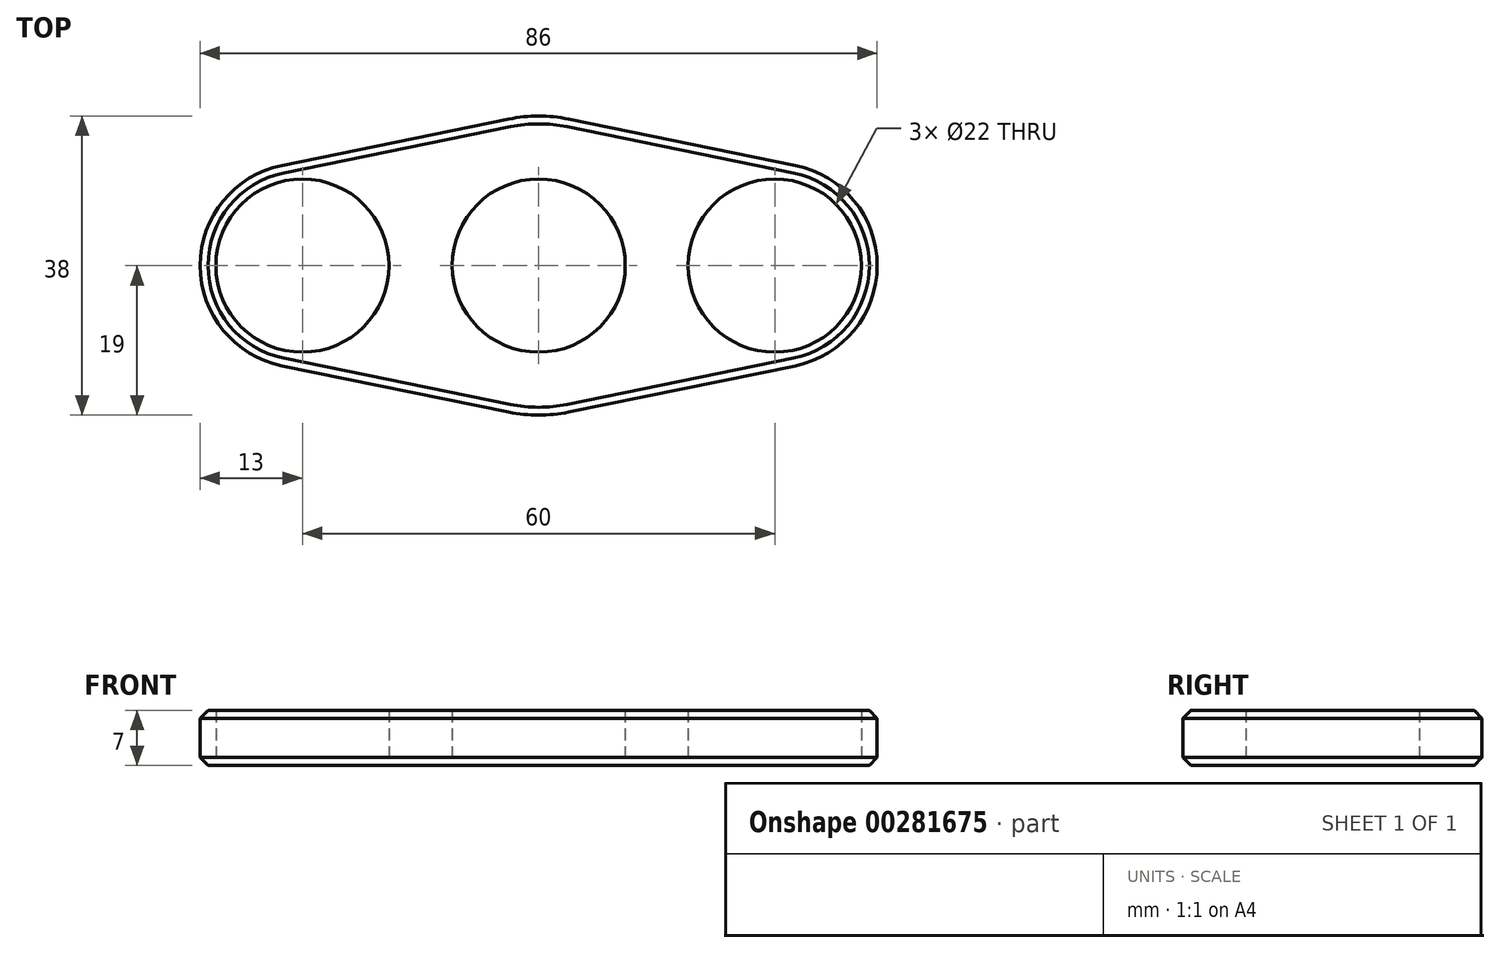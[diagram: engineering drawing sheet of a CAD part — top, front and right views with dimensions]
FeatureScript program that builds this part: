
annotation { "Feature Type Name" : "Feature", "Feature Type Description" : "" }
export const myFeature = defineFeature(function(context is Context, id is Id, definition is map)
    precondition{}
    {
        {
            var Q0;
            Q0=qCreatedBy(makeId("Top.planeOp"),FACE);
            var sketch = newSketch(context, id + "F0", { "sketchPlane" : qUnion([Q0])});
            skCircle(sketch, "E0", {"center": v(0, 0) * mm, "radius": 11 * mm});
            skCircle(sketch, "E1", {"center": v(30, 0) * mm, "radius": 11 * mm});
            skCircle(sketch, "E2", {"center": v(-30, 0) * mm, "radius": 11 * mm});
            skArc(sketch, "E3", {"start": v(32.6, -12.74) * mm, "mid": v(43, 0) * mm, "end": v(32.6, 12.74) * mm});
            skArc(sketch, "E4", {"start": v(-32.6, 12.74) * mm, "mid": v(-43, 0) * mm, "end": v(-32.6, -12.74) * mm});
            skArc(sketch, "E5", {"start": v(-3.8, -18.62) * mm, "mid": v(0, -19) * mm, "end": v(3.8, -18.62) * mm});
            skLineSegment(sketch, "E6", {"start": v(-32.6, 12.74) * mm, "end": v(-3.8, 18.62) * mm});
            skLineSegment(sketch, "E7", {"start": v(3.8, 18.62) * mm, "end": v(32.6, 12.74) * mm});
            skLineSegment(sketch, "E8", {"start": v(-32.6, -12.74) * mm, "end": v(-3.8, -18.62) * mm});
            skLineSegment(sketch, "E9", {"start": v(32.6, -12.74) * mm, "end": v(3.8, -18.62) * mm});
            skArc(sketch, "E10.trimOffspring", {"start": v(3.8, 18.62) * mm, "mid": v(0, 19) * mm, "end": v(-3.8, 18.62) * mm});
            skSolve(sketch);
        }
        {
            var Q0;
            Q0=makeQuery(id+"F0.imprint","IMPRINT",FACE,{"disambiguationData":[TD([[makeQuery(id+"F0.imprint","IMPRINT",EDGE,{"derivedFrom":sQuery(id+"F0.wireOp",EDGE,"E0")}),-1.0]])]});
            extrude(context, id + "F1", {"entities" : qUnion([Q0]), "depth" : 7 * mm});
        }
        {
            var Q0;
            Q0=makeQuery(id+"F1.opExtrude","CAP_EDGE",EDGE,{"disambiguationData":[OSD([sQuery(id+"F0.wireOp",EDGE,"E3")])],"isStart":false});
            var Q1;
            Q1=makeQuery(id+"F1.opExtrude","CAP_EDGE",EDGE,{"disambiguationData":[OSD([sQuery(id+"F0.wireOp",EDGE,"E3")])],"isStart":true});
            chamfer(context, id + "F2", {"entities" : qUnion([Q0, Q1]), "width" : 1 * mm, "tangentPropagation" : true});
        }
    });
